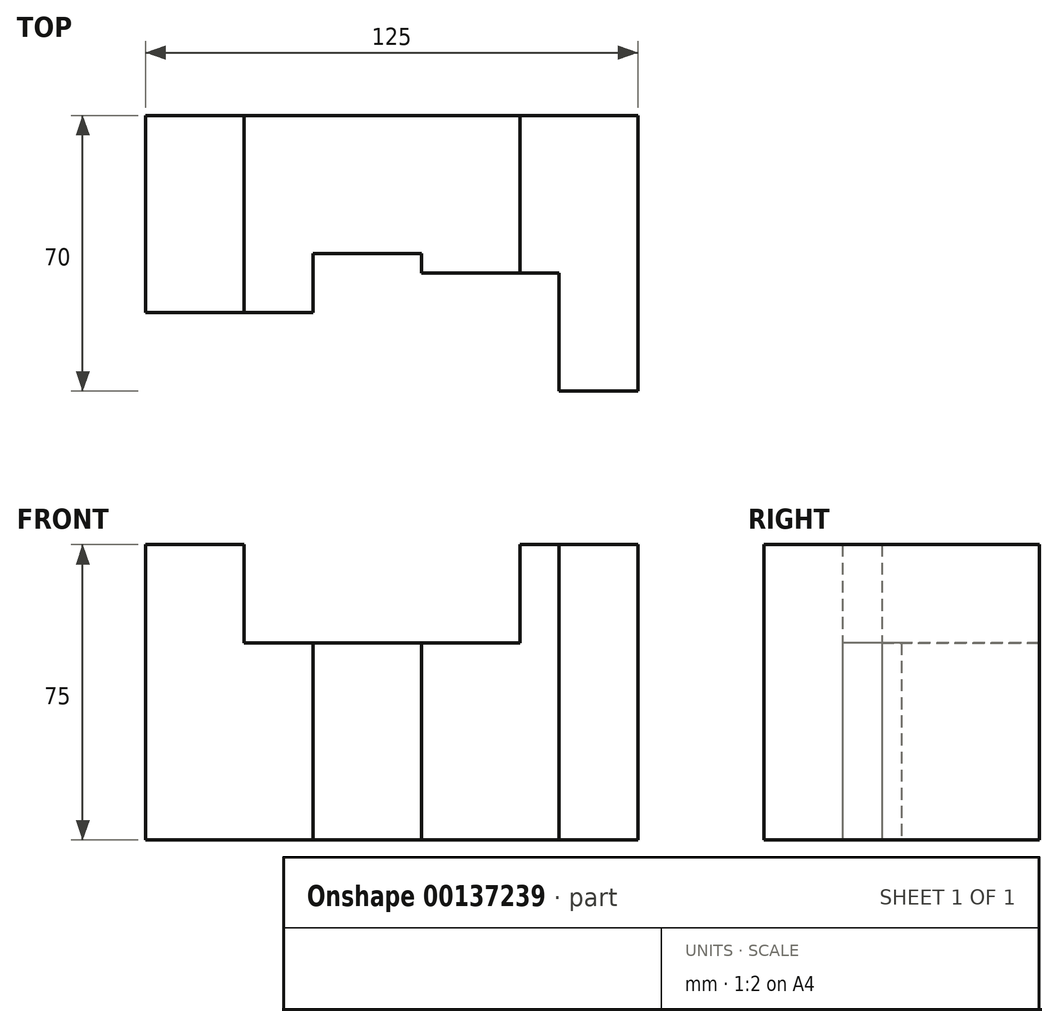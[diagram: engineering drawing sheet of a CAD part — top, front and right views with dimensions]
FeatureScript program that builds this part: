
annotation { "Feature Type Name" : "Feature", "Feature Type Description" : "" }
export const myFeature = defineFeature(function(context is Context, id is Id, definition is map)
    precondition{}
    {
        {
            var Q0;
            Q0=qCreatedBy(makeId("Top.planeOp"),FACE);
            var sketch = newSketch(context, id + "F0", { "sketchPlane" : qUnion([Q0])});
            skLineSegment(sketch, "E0", {"start": v(0, -50) * mm, "end": v(0, 0) * mm});
            skLineSegment(sketch, "E1", {"start": v(0, 0) * mm, "end": v(125, 0) * mm});
            skLineSegment(sketch, "E2", {"start": v(125, 0) * mm, "end": v(125, -70) * mm});
            skLineSegment(sketch, "E3", {"start": v(125, -70) * mm, "end": v(105, -70) * mm});
            skLineSegment(sketch, "E4", {"start": v(105, -70) * mm, "end": v(105, -40) * mm});
            skLineSegment(sketch, "E5", {"start": v(105, -40) * mm, "end": v(70, -40) * mm});
            skLineSegment(sketch, "E6", {"start": v(70, -40) * mm, "end": v(70, -35) * mm});
            skLineSegment(sketch, "E7", {"start": v(70, -35) * mm, "end": v(42.5, -35) * mm});
            skLineSegment(sketch, "E8", {"start": v(42.5, -35) * mm, "end": v(42.5, -50) * mm});
            skLineSegment(sketch, "E9", {"start": v(42.5, -50) * mm, "end": v(0, -50) * mm});
            skLineSegment(sketch, "E10", {"start": v(25, 0) * mm, "end": v(25, -50) * mm});
            skLineSegment(sketch, "E11", {"start": v(95, -40) * mm, "end": v(95, 0) * mm});
            skSolve(sketch);
        }
        {
            var Q0;
            {var subQ0=sQuery(id+"F0.wireOp",EDGE,"E0");Q0=makeQuery(id+"F0.imprint","IMPRINT",FACE,{"disambiguationData":[TD([[makeQuery(id+"F0.imprint","IMPRINT",EDGE,{"derivedFrom":subQ0}),-1.0]])]});}
            var Q1;
            {var subQ1=sQuery(id+"F0.wireOp",EDGE,"E2");Q1=makeQuery(id+"F0.imprint","IMPRINT",FACE,{"disambiguationData":[TD([[makeQuery(id+"F0.imprint","IMPRINT",EDGE,{"derivedFrom":subQ1}),-1.0]])]});}
            extrude(context, id + "F1", {"entities" : qUnion([Q0, Q1]), "depth" : 75 * mm});
        }
        {
            var Q0;
            {var subQ0=sQuery(id+"F0.wireOp",EDGE,"E6");Q0=makeQuery(id+"F0.imprint","IMPRINT",FACE,{"disambiguationData":[TD([[makeQuery(id+"F0.imprint","IMPRINT",EDGE,{"derivedFrom":subQ0}),-1.0]])]});}
            extrude(context, id + "F2", {"entities" : qUnion([Q0]), "operationType" : NewBodyOperationType.ADD, "depth" : 50 * mm});
        }
    });
